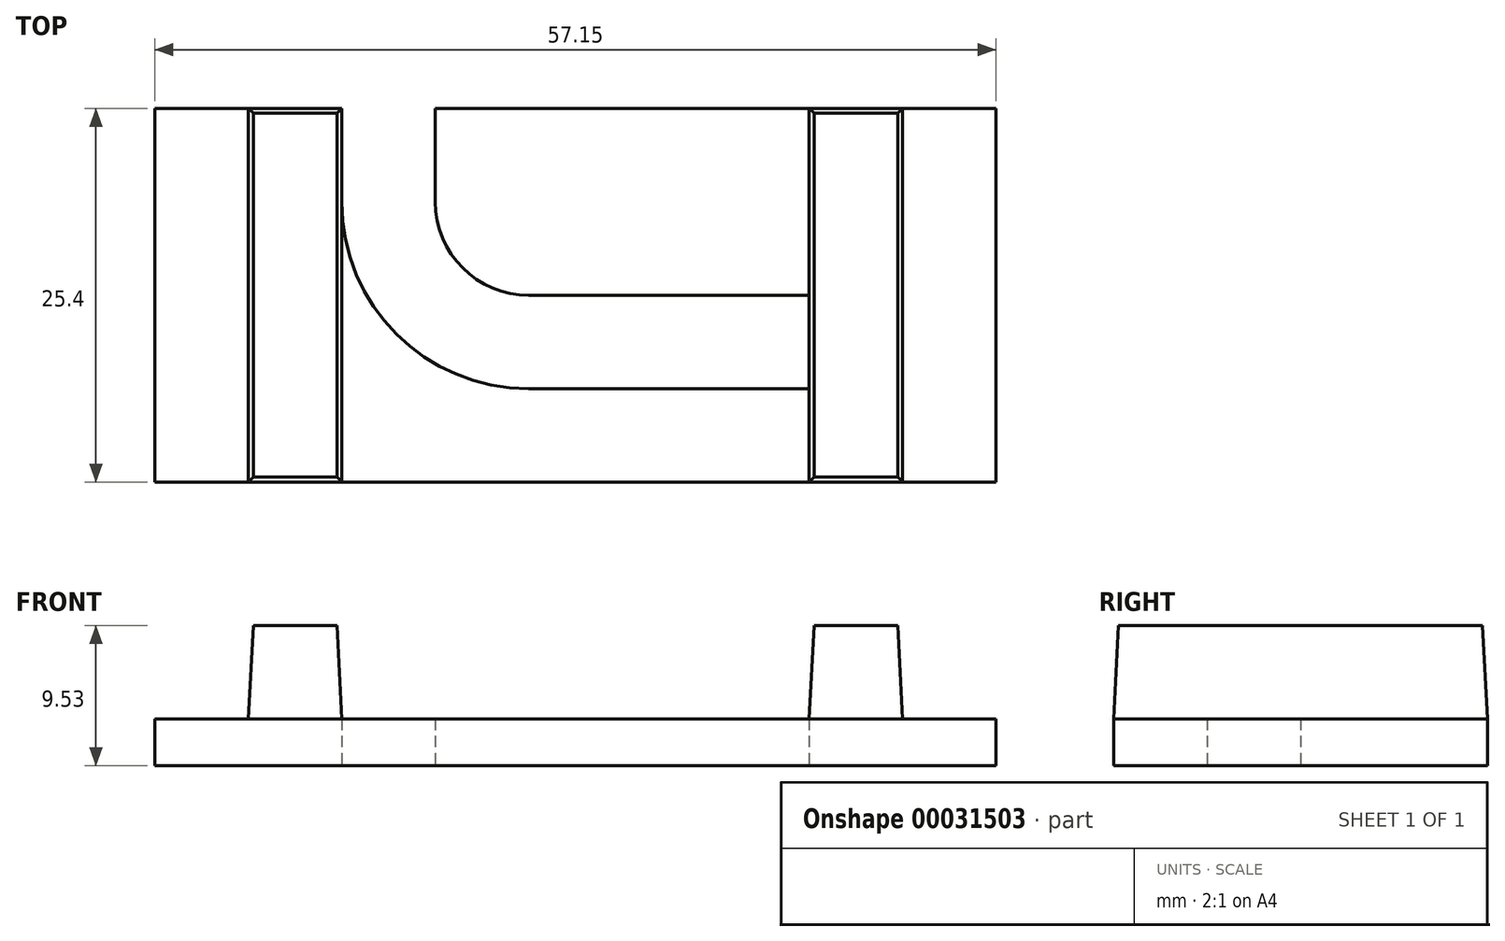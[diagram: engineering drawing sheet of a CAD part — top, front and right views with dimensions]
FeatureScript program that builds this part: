
annotation { "Feature Type Name" : "Feature", "Feature Type Description" : "" }
export const myFeature = defineFeature(function(context is Context, id is Id, definition is map)
    precondition{}
    {
        {
            var Q0;
            Q0=qCreatedBy(makeId("Top.planeOp"),FACE);
            var sketch = newSketch(context, id + "F0", { "sketchPlane" : qUnion([Q0])});
            skLineSegment(sketch, "E0.bottom", {"start": v(-45.79, -4.66) * mm, "end": v(11.36, -4.66) * mm});
            skLineSegment(sketch, "E0.top", {"start": v(-45.79, 20.74) * mm, "end": v(-33.09, 20.74) * mm});
            skLineSegment(sketch, "E0.left", {"start": v(-45.79, -4.66) * mm, "end": v(-45.79, 20.74) * mm});
            skLineSegment(sketch, "E0.right", {"start": v(11.36, -4.66) * mm, "end": v(11.36, 20.74) * mm});
            skLineSegment(sketch, "E1.left", {"start": v(-33.09, 20.74) * mm, "end": v(-33.09, 14.4) * mm});
            skLineSegment(sketch, "E1.right", {"start": v(-26.74, 20.74) * mm, "end": v(-26.74, 14.4) * mm});
            skLineSegment(sketch, "E2.bottom", {"start": v(-20.39, 1.7) * mm, "end": v(-1.34, 1.7) * mm});
            skLineSegment(sketch, "E2.top", {"start": v(-20.39, 8.04) * mm, "end": v(-1.34, 8.04) * mm});
            skLineSegment(sketch, "E2.right", {"start": v(-1.34, 1.7) * mm, "end": v(-1.34, 8.04) * mm});
            skLineSegment(sketch, "E3.trimOffspring", {"start": v(-26.74, 20.74) * mm, "end": v(11.36, 20.74) * mm});
            skPoint(sketch, "E4.visualSharp", {"position": v(-33.09, 1.7) * mm});
            skArc(sketch, "E4.filletArc", {"start": v(-33.09, 14.4) * mm, "mid": v(-29.37, 5.4) * mm, "end": v(-20.39, 1.7) * mm});
            skPoint(sketch, "E5.visualSharp", {"position": v(-26.74, 8.04) * mm});
            skArc(sketch, "E5.filletArc", {"start": v(-26.74, 14.4) * mm, "mid": v(-24.88, 9.9) * mm, "end": v(-20.39, 8.04) * mm});
            skSolve(sketch);
        }
        {
            var Q0;
            Q0=makeQuery(id+"F0.imprint","IMPRINT",FACE,{"disambiguationData":[TD([[makeQuery(id+"F0.imprint","IMPRINT",EDGE,{"derivedFrom":sQuery(id+"F0.wireOp",EDGE,"E0.bottom")}),1.0]])]});
            extrude(context, id + "F1", {"entities" : qUnion([Q0]), "depth" : 3.17 * mm});
        }
        {
            var Q0;
            Q0=makeQuery(id+"F1.opExtrude","CAP_FACE",FACE,{"disambiguationData":[OSD([sQuery(id+"F0.wireOp",EDGE,"E0.bottom"),sQuery(id+"F0.wireOp",EDGE,"E0.top"),sQuery(id+"F0.wireOp",EDGE,"E0.left"),sQuery(id+"F0.wireOp",EDGE,"E0.right"),sQuery(id+"F0.wireOp",EDGE,"E1.left"),sQuery(id+"F0.wireOp",EDGE,"E1.right"),sQuery(id+"F0.wireOp",EDGE,"E2.bottom"),sQuery(id+"F0.wireOp",EDGE,"E2.top"),sQuery(id+"F0.wireOp",EDGE,"E2.right"),sQuery(id+"F0.wireOp",EDGE,"E3.trimOffspring"),sQuery(id+"F0.wireOp",EDGE,"E4.filletArc"),sQuery(id+"F0.wireOp",EDGE,"E5.filletArc")])],"isStart":false});
            var sketch = newSketch(context, id + "F2", { "sketchPlane" : qUnion([Q0])});
            skLineSegment(sketch, "E6.bottom", {"start": v(-39.44, 20.74) * mm, "end": v(-33.09, 20.74) * mm});
            skLineSegment(sketch, "E6.top", {"start": v(-39.44, -4.66) * mm, "end": v(-33.09, -4.66) * mm});
            skLineSegment(sketch, "E6.left", {"start": v(-39.44, 20.74) * mm, "end": v(-39.44, -4.66) * mm});
            skLineSegment(sketch, "E6.right", {"start": v(-33.09, 20.74) * mm, "end": v(-33.09, -4.66) * mm});
            skLineSegment(sketch, "E7.bottom", {"start": v(5.01, 20.74) * mm, "end": v(-1.34, 20.74) * mm});
            skLineSegment(sketch, "E7.top", {"start": v(5.01, -4.66) * mm, "end": v(-1.34, -4.66) * mm});
            skLineSegment(sketch, "E7.left", {"start": v(5.01, 20.74) * mm, "end": v(5.01, -4.66) * mm});
            skLineSegment(sketch, "E7.right", {"start": v(-1.34, 20.74) * mm, "end": v(-1.34, -4.66) * mm});
            skSolve(sketch);
        }
        {
            var Q0;
            {var subQ2=sQuery(id+"F2.wireOp",EDGE,"E6.bottom");Q0=makeQuery(id+"F2.imprint","IMPRINT",FACE,{"disambiguationData":[TD([[makeQuery(id+"F2.imprint","IMPRINT",EDGE,{"derivedFrom":subQ2}),-1.0]])]});}
            var Q1;
            {var subQ4=sQuery(id+"F2.wireOp",EDGE,"E7.bottom");Q1=makeQuery(id+"F2.imprint","IMPRINT",FACE,{"disambiguationData":[TD([[makeQuery(id+"F2.imprint","IMPRINT",EDGE,{"derivedFrom":subQ4}),-1.0]])]});}
            extrude(context, id + "F3", {"entities" : qUnion([Q0, Q1]), "operationType" : NewBodyOperationType.ADD, "depth" : 6.35 * mm, "hasDraft" : true, "draftAngle" : 3 * degree, "draftPullDirection" : true});
        }
    });
